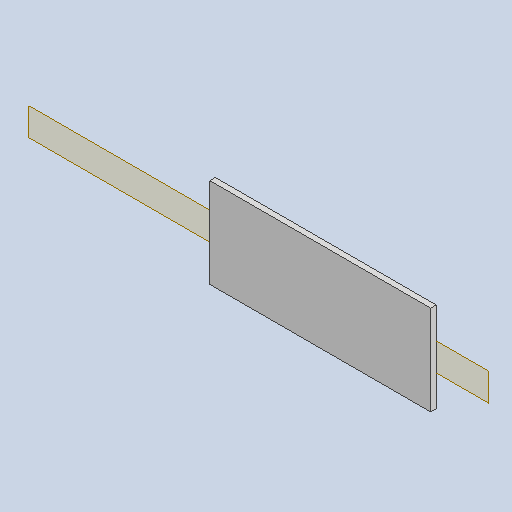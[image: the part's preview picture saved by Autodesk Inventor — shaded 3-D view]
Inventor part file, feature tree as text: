
AUTODESK INVENTOR PART (.ipt)
format: ipt  version: 2023 (Build 270158000, 158)  size: 101,376 bytes
history: native  units: mm
features: other x6, plane x1, sketch x1, reference x1
ambient origin geometry x8: Origin, YZ Plane, XZ Plane, XY Plane, X Axis, Y Axis, Z Axis, Center Point
bodies: Body1 (feature_tree)
feature tree (9):
  other  "Sólido1"
  plane  "Plano de trabajo1"
  other  "Cara1"
  sketch  "Boceto1"  dims[d0=50.0mm d1=7.0mm]
  reference  "Referencia1"
  other  "Placa1"
  other  "<userpath>\OneDrive\PLANOS\OREJA DE IZAJE\OREJA_DE_IZAJE.iam"
  other  "OREJA_DE_IZAJE.iam"
  other  "OREJA_DE_IZAJE:1"
